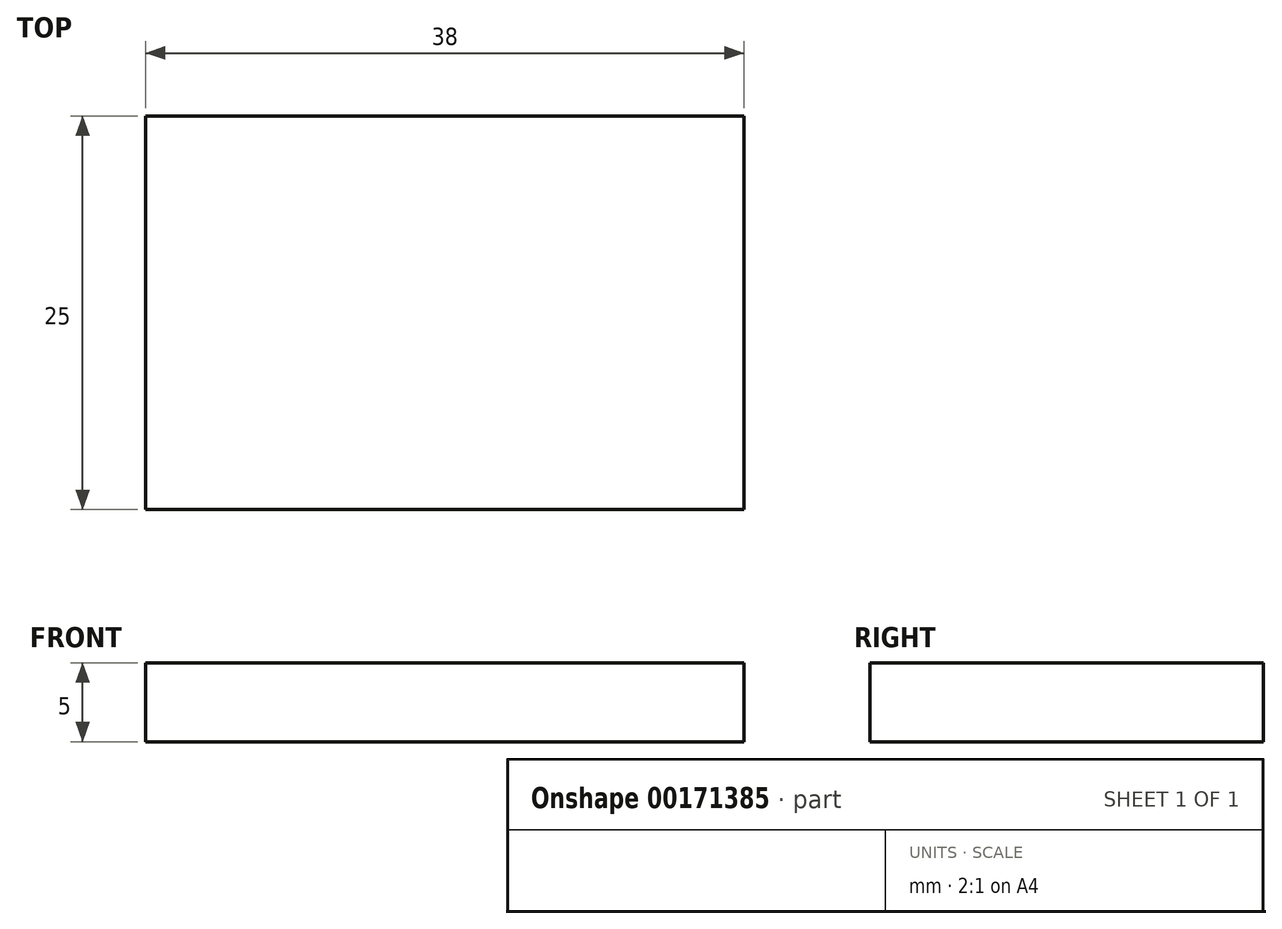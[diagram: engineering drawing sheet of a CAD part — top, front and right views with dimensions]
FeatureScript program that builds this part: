
annotation { "Feature Type Name" : "Feature", "Feature Type Description" : "" }
export const myFeature = defineFeature(function(context is Context, id is Id, definition is map)
    precondition{}
    {
        {
            var Q0;
            Q0=qCreatedBy(makeId("Top.planeOp"),FACE);
            var sketch = newSketch(context, id + "F0", { "sketchPlane" : qUnion([Q0])});
            skLineSegment(sketch, "E0.bottom", {"start": v(-19, 12.5) * mm, "end": v(19, 12.5) * mm});
            skLineSegment(sketch, "E0.top", {"start": v(-19, -12.5) * mm, "end": v(19, -12.5) * mm});
            skLineSegment(sketch, "E0.left", {"start": v(-19, 12.5) * mm, "end": v(-19, -12.5) * mm});
            skLineSegment(sketch, "E0.right", {"start": v(19, 12.5) * mm, "end": v(19, -12.5) * mm});
            skPoint(sketch, "E0.middle", {"position": v(0, 0) * mm});
            skSolve(sketch);
        }
        {
            var Q0;
            Q0 = qSketchRegion(id + "F0", true);
            extrude(context, id + "F1", {"entities" : qUnion([Q0]), "endBound" : BoundingType.SYMMETRIC, "depth" : 5 * mm});
        }
    });
